# Revit family: SPG-105_RFA
name_source: partatom
category: Aparatos sanitarios
units: mm (PartAtom-declared; Revit-internal decimal feet)

## family parameters
Activar corte en vistas = No
Compartido = No
Corte con vacíos al cargar = No
Cota de conector redondo = Usar diámetro
Mantener orientación de anotación = No
Número OmniClass = 23.45.00.00
Punto de cálculo de habitación = No
Se basa en plano de trabajo = No
Siempre vertical = Sí
Tipo de pieza = Normal
Título OmniClass = Sanitary, Laundry, and Cleaning Equipment

## types (1)
- SPG-105
    Brass Chromed = Brass
    Comentarios de tipo = Accessories
    Descripción = Toallero de barra Spiga.
    Elevación por defecto = 0"
    Fabricante = HELVEX
    Features = Toallero de barra que armoniza con la colección de la línea de acceorios Spiga. CARGA MÁXIMA: 10 kg. en instalación en muro, para tablaroca es
necesario añadir un refuerzo de madera.
Fácil de instalar.
    Imagen de tipo = <Ninguno>
    Modelo = SPG-05
    Total Depth = 3"
    Total Height = 1"
    Total Length = 20"

## geometry (parser evidence)
native form markers: Sweep x3
no freeform markers — native parametric forms only
